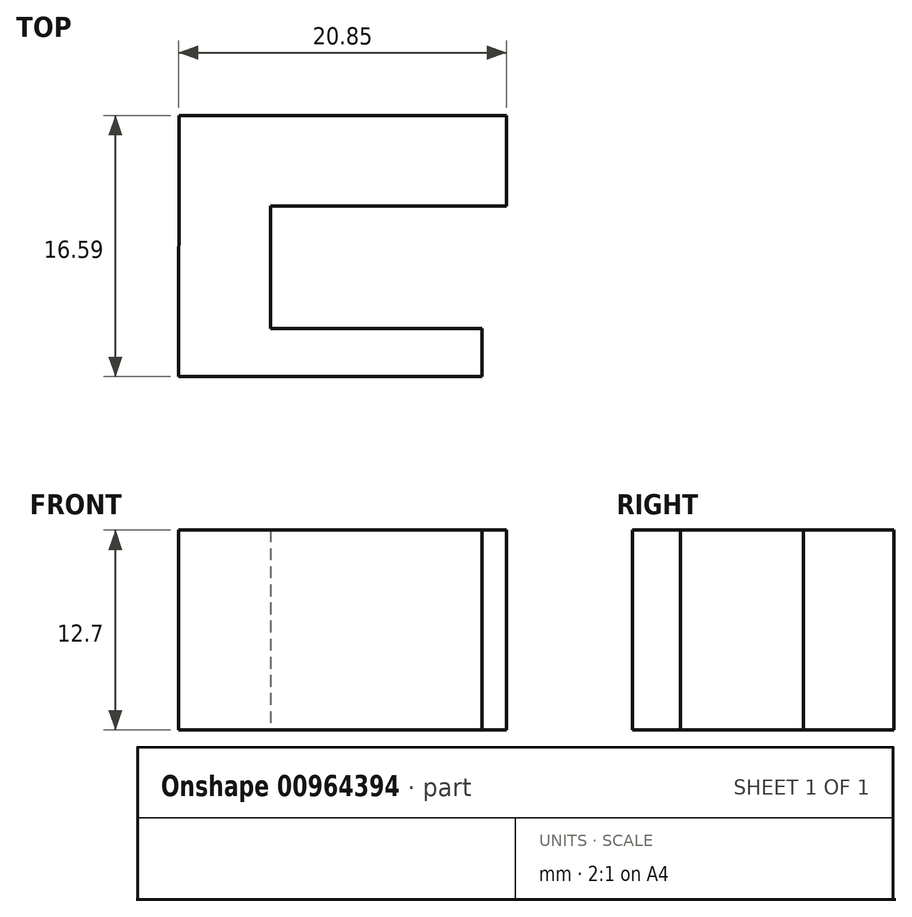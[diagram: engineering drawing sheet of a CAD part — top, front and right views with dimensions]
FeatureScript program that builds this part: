
annotation { "Feature Type Name" : "Feature", "Feature Type Description" : "" }
export const myFeature = defineFeature(function(context is Context, id is Id, definition is map)
    precondition{}
    {
        {
            var Q0;
            Q0=qCreatedBy(makeId("Top.planeOp"),FACE);
            var sketch = newSketch(context, id + "F0", { "sketchPlane" : qUnion([Q0])});
            skLineSegment(sketch, "E0", {"start": v(8.19, 26.74) * mm, "end": v(28.99, 26.74) * mm});
            skLineSegment(sketch, "E1", {"start": v(28.99, 26.74) * mm, "end": v(28.99, 20.99) * mm});
            skLineSegment(sketch, "E2", {"start": v(28.99, 20.99) * mm, "end": v(13.98, 20.99) * mm});
            skLineSegment(sketch, "E3", {"start": v(13.98, 20.99) * mm, "end": v(13.98, 13.2) * mm});
            skLineSegment(sketch, "E4", {"start": v(13.98, 13.2) * mm, "end": v(27.41, 13.2) * mm});
            skLineSegment(sketch, "E5", {"start": v(27.41, 13.2) * mm, "end": v(27.41, 10.15) * mm});
            skLineSegment(sketch, "E6", {"start": v(27.41, 10.15) * mm, "end": v(8.14, 10.15) * mm});
            skLineSegment(sketch, "E7", {"start": v(8.14, 10.15) * mm, "end": v(8.19, 26.74) * mm});
            skSolve(sketch);
        }
        {
            var Q0;
            Q0=makeQuery(id+"F0.imprint","IMPRINT",FACE,{"disambiguationData":[TD([[makeQuery(id+"F0.imprint","IMPRINT",EDGE,{"derivedFrom":sQuery(id+"F0.wireOp",EDGE,"E0")}),-1.0]])]});
            extrude(context, id + "F1", {"entities" : qUnion([Q0]), "depth" : 12.7 * mm, "offsetDistance" : 25.4 * mm});
        }
    });
